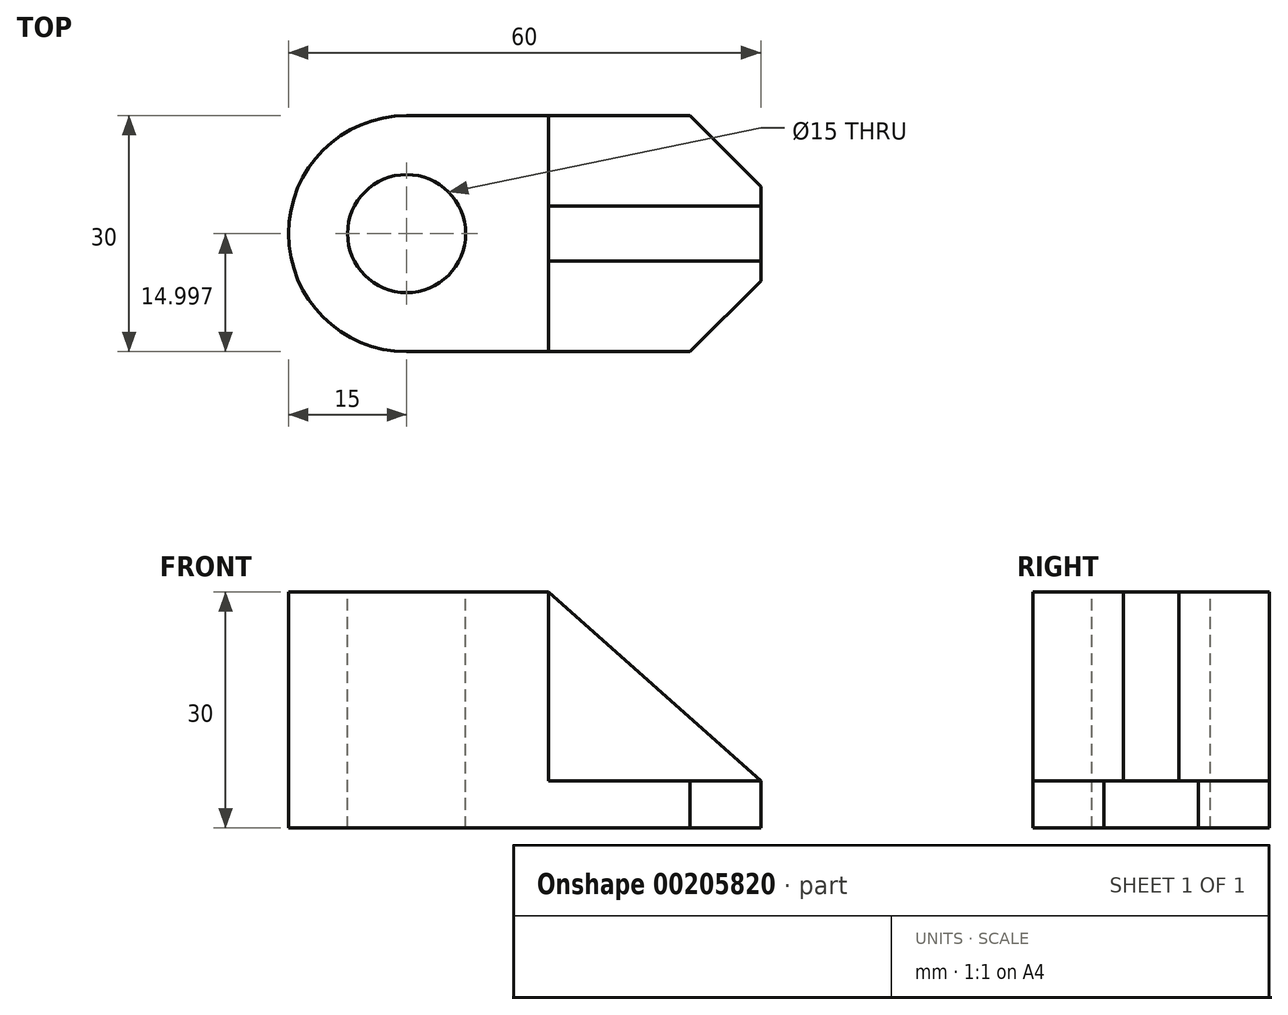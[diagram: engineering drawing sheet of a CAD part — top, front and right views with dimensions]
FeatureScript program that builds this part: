
annotation { "Feature Type Name" : "Feature", "Feature Type Description" : "" }
export const myFeature = defineFeature(function(context is Context, id is Id, definition is map)
    precondition{}
    {
        {
            var Q0;
            Q0=qCreatedBy(makeId("Top.planeOp"),FACE);
            var sketch = newSketch(context, id + "F0", { "sketchPlane" : qUnion([Q0])});
            skLineSegment(sketch, "E0.bottom", {"start": v(-30, 15.99) * mm, "end": v(30, 15.99) * mm});
            skLineSegment(sketch, "E0.top", {"start": v(-30, -14.01) * mm, "end": v(30, -14.01) * mm});
            skLineSegment(sketch, "E0.left", {"start": v(-30, 15.99) * mm, "end": v(-30, -14.01) * mm});
            skLineSegment(sketch, "E0.right", {"start": v(30, 15.99) * mm, "end": v(30, -14.01) * mm});
            skPoint(sketch, "E0.middle", {"position": v(0, 0.99) * mm});
            skSolve(sketch);
        }
        {
            var Q0;
            Q0=makeQuery(id+"F0.imprint","IMPRINT",FACE,{"disambiguationData":[TD([[makeQuery(id+"F0.imprint","IMPRINT",EDGE,{"derivedFrom":sQuery(id+"F0.wireOp",EDGE,"E0.bottom")}),-1.0]])]});
            extrude(context, id + "F1", {"entities" : qUnion([Q0]), "depth" : 30 * mm, "offsetDistance" : 25 * mm});
        }
        {
            var Q0;
            Q0=makeQuery(id+"F1.opExtrude","SWEPT_EDGE",EDGE,{"disambiguationData":[OSD([sQuery(id+"F0.wireOp",EDGE,"E0.top"),sQuery(id+"F0.wireOp",EDGE,"E0.left")])]});
            var Q1;
            Q1=makeQuery(id+"F1.opExtrude","SWEPT_EDGE",EDGE,{"disambiguationData":[OSD([sQuery(id+"F0.wireOp",EDGE,"E0.bottom"),sQuery(id+"F0.wireOp",EDGE,"E0.left")])]});
            fillet(context, id + "F2", {"entities" : qUnion([Q0, Q1]), "radius" : 15 * mm, "tangentPropagation" : true, "allowEdgeOverflow" : false});
        }
        {
            var Q0;
            Q0=makeQuery(id+"F1.opExtrude","SWEPT_EDGE",EDGE,{"disambiguationData":[OSD([sQuery(id+"F0.wireOp",EDGE,"E0.top"),sQuery(id+"F0.wireOp",EDGE,"E0.right")])]});
            var Q1;
            Q1=makeQuery(id+"F1.opExtrude","SWEPT_EDGE",EDGE,{"disambiguationData":[OSD([sQuery(id+"F0.wireOp",EDGE,"E0.bottom"),sQuery(id+"F0.wireOp",EDGE,"E0.right")])]});
            chamfer(context, id + "F3", {"entities" : qUnion([Q0, Q1]), "width" : 9 * mm, "tangentPropagation" : true});
        }
        {
            var Q0;
            Q0=makeQuery(id+"F1.opExtrude","CAP_FACE",FACE,{"disambiguationData":[OSD([sQuery(id+"F0.wireOp",EDGE,"E0.bottom"),sQuery(id+"F0.wireOp",EDGE,"E0.top"),sQuery(id+"F0.wireOp",EDGE,"E0.left"),sQuery(id+"F0.wireOp",EDGE,"E0.right")])],"isStart":false});
            var sketch = newSketch(context, id + "F4", { "sketchPlane" : qUnion([Q0])});
            skCircle(sketch, "E1", {"center": v(-15, 0.99) * mm, "radius": 7.5 * mm});
            skSolve(sketch);
        }
        {
            var Q0;
            Q0=makeQuery(id+"F4.imprint","IMPRINT",FACE,{"disambiguationData":[TD([[makeQuery(id+"F4.imprint","IMPRINT",EDGE,{"derivedFrom":sQuery(id+"F4.wireOp",EDGE,"E1")}),1.0]])]});
            extrude(context, id + "F5", {"entities" : qUnion([Q0]), "operationType" : NewBodyOperationType.REMOVE, "endBound" : BoundingType.UP_TO_NEXT, "oppositeDirection" : true, "depth" : 25 * mm, "offsetDistance" : 25 * mm});
        }
        {
            var Q0;
            Q0=makeQuery(id+"F1.opExtrude","SWEPT_FACE",FACE,{"disambiguationData":[OSD([sQuery(id+"F0.wireOp",EDGE,"E0.top")])]});
            var sketch = newSketch(context, id + "F6", { "sketchPlane" : qUnion([Q0])});
            skLineSegment(sketch, "E2.bottom", {"start": v(3, 30) * mm, "end": v(30, 30) * mm});
            skLineSegment(sketch, "E2.top", {"start": v(3, 6) * mm, "end": v(30, 6) * mm});
            skLineSegment(sketch, "E2.left", {"start": v(3, 30) * mm, "end": v(3, 6) * mm});
            skLineSegment(sketch, "E2.right", {"start": v(30, 30) * mm, "end": v(30, 6) * mm});
            skSolve(sketch);
        }
        {
            var Q0;
            {var subQ4=sQuery(id+"F6.wireOp",EDGE,"E2.right");Q0=makeQuery(id+"F6.imprint","IMPRINT",FACE,{"disambiguationData":[TD([[makeQuery(id+"F6.imprint","IMPRINT",EDGE,{"derivedFrom":subQ4}),-1.0]])]});}
            var Q1;
            {var subQ4=sQuery(id+"F6.wireOp",EDGE,"E2.left");Q1=makeQuery(id+"F6.imprint","IMPRINT",FACE,{"disambiguationData":[TD([[makeQuery(id+"F6.imprint","IMPRINT",EDGE,{"derivedFrom":subQ4}),1.0]])]});}
            extrude(context, id + "F7", {"entities" : qUnion([Q0, Q1]), "operationType" : NewBodyOperationType.REMOVE, "oppositeDirection" : true, "depth" : (15 - 3.5) * mm, "offsetDistance" : 25 * mm});
        }
        {
            var Q0;
            Q0 = qSketchRegion(id + "F6", true);
            extrude(context, id + "F8", {"entities" : qUnion([Q0]), "operationType" : NewBodyOperationType.REMOVE, "endBound" : BoundingType.THROUGH_ALL, "oppositeDirection" : true, "depth" : 36.9 * mm, "offsetDistance" : 25 * mm, "hasSecondDirection" : true, "secondDirectionOppositeDirection" : true, "secondDirectionDepth" : (15 + 3.5) * mm});
        }
        {
            var Q0;
            Q0=makeQuery(id+"F7.boolean.opBoolean","COPY",FACE,{"derivedFrom":makeQuery(id+"F7.opExtrude","CAP_FACE",FACE,{"disambiguationData":[OSD([sQuery(id+"F6.wireOp",EDGE,"E2.bottom"),sQuery(id+"F6.wireOp",EDGE,"E2.top"),sQuery(id+"F6.wireOp",EDGE,"E2.left"),sQuery(id+"F6.wireOp",EDGE,"E2.right")])],"isStart":false})});
            var sketch = newSketch(context, id + "F9", { "sketchPlane" : qUnion([Q0])});
            skLineSegment(sketch, "E3", {"start": v(30, 6) * mm, "end": v(3, 30) * mm});
            skLineSegment(sketch, "E4", {"start": v(3, 30) * mm, "end": v(30, 30) * mm});
            skLineSegment(sketch, "E5", {"start": v(30, 30) * mm, "end": v(30, 6) * mm});
            skSolve(sketch);
        }
        {
            var Q0;
            Q0=makeQuery(id+"F9.imprint","IMPRINT",FACE,{"disambiguationData":[TD([[makeQuery(id+"F9.imprint","IMPRINT",EDGE,{"derivedFrom":sQuery(id+"F9.wireOp",EDGE,"E3")}),-1.0]])]});
            extrude(context, id + "F10", {"entities" : qUnion([Q0]), "operationType" : NewBodyOperationType.REMOVE, "endBound" : BoundingType.UP_TO_NEXT, "oppositeDirection" : true, "depth" : 25 * mm, "offsetDistance" : 25 * mm});
        }
    });
